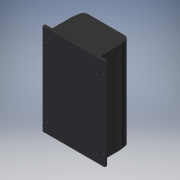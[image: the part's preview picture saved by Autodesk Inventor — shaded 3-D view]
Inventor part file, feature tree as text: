
AUTODESK INVENTOR PART (.ipt)
format: ipt  version: 2018 (Build 220112000, 112)  size: 145,408 bytes
history: native  units: mm
features: fillet x3, sketch x3, extrude x2, hole x1
ambient origin geometry x8: Origin, YZ Plane, XZ Plane, XY Plane, X Axis, Y Axis, Z Axis, Center Point
bodies: Solid1 (feature_tree)
feature tree (9):
  extrude  "Extrusion1"  Depth=2.9mm
  fillet  "Fillet1"  Radius=115.0mm
  fillet  "Fillet2"  Radius=25.0mm
  hole  "Hole1"  [1 undecoded]
  extrude  "Extrusion2"  Depth=20.0mm
  fillet  "Fillet3"  Radius=13.75mm
  sketch  "Sketch1"  dims[d0=77.8mm d1=2.9mm d4=115.0mm d5=0.0mm d6=25.0mm]
  sketch  "Sketch2"  dims[d7=56.0mm d8=41.0mm]
  sketch  "Sketch3"  dims[d9=5.75mm d10=20.0mm d11=13.75mm d12=4.0mm d13=4.0mm d14=14.0mm d15=4.7mm d16=6.0mm d17=4.0mm d18=2.0mm d19=90.0deg d20=8.0mm d21=20.594885mm d22=4.85mm d23=4.85mm d24=6.0mm d25=12.7mm d26=6.5mm d27=0.0mm d28=2.25mm]
note: 1 required parameter value undecoded (feature->parameter linkage not recoverable at this tier; creation-order binding heuristic only, values carry confidence <= 0.55)
